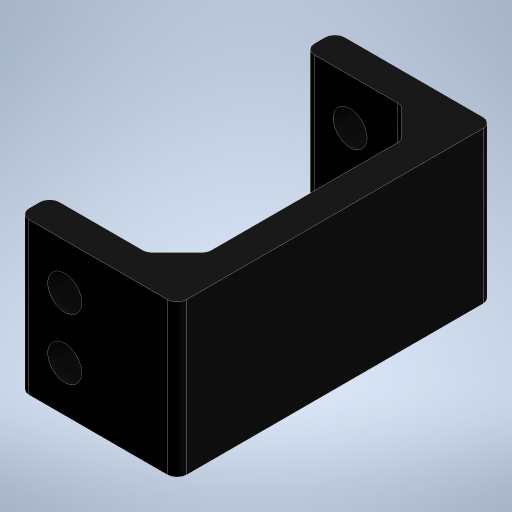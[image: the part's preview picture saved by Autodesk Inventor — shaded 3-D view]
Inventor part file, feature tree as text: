
AUTODESK INVENTOR PART (.ipt)
format: ipt  version: 2024.2 (Build 282272000, 272)  size: 241,152 bytes
history: native  units: mm
features: extrude x2, other x1, sketch x1, chamfer x1, fillet x1
ambient origin geometry x8: Origin, YZ Plane, XZ Plane, XY Plane, X Axis, Y Axis, Z Axis, Center Point
bodies: Body1 (feature_tree)
feature tree (6):
  other  "Bryła1"
  sketch  "Szkic1"
  extrude  "Wyciągnięcie proste1"  Depth=21.0mm
  extrude  "Wyciągnięcie proste2"  Depth=25.0mm
  chamfer  "Faza1"  Distance=5.0mm
  fillet  "Zaokrąglenie1"  Radius=7.5mm
